FCSTD DOCUMENT  (FreeCAD 0.18R)
Label: StaveBracket
License: All rights reserved
LicenseURL: http://en.wikipedia.org/wiki/All_rights_reserved
objects: Sketcher::SketchObject×1
note: 1 computed .brp shape members not serialized (recipe doc carries the construction recipe); baked Part::Feature solids carry a one-line shape summary decoded from their .brp

FEATURE [Sketcher::SketchObject] Sketch  label="Sketch-Bracket"
  MapMode = 5
  expr: Constraints[64] = Constraints.b * 10
  expr: Constraints[61] = (Constraints.b - Constraints.bar_maj) * (2 - (1 + sqrt(5)) / 2)
  expr: Constraints.square = Constraints.b / (2 - (1 + sqrt(5)) / 2)
  expr: Constraints.bar_maj = Constraints.b * 2 / (1 + sqrt(5))
  sketch-geometry (26):
    g0: LineSegment [constr] StartX=-0.381966 StartY=1.8e-15 StartZ=0 EndX=0.618034 EndY=1.8e-15 EndZ=0
    g1: LineSegment [constr] StartX=0.618034 StartY=1.8e-15 StartZ=0 EndX=0 EndY=1.8e-15 EndZ=0
    g2: LineSegment StartX=-0.381966 StartY=1.8e-15 StartZ=0 EndX=-0.381966 EndY=1 EndZ=0
    g3: LineSegment [constr] StartX=-0.381966 StartY=1.8e-15 StartZ=0 EndX=2.23607 EndY=1.8e-15 EndZ=0
    g4: LineSegment [constr] StartX=2.23607 StartY=1.8e-15 StartZ=0 EndX=2.23607 EndY=2.61803 EndZ=0
    g5: LineSegment [constr] StartX=2.23607 StartY=2.61803 StartZ=0 EndX=-0.381966 EndY=2.61803 EndZ=0
    g6: LineSegment [constr] StartX=-0.381966 StartY=2.61803 StartZ=0 EndX=-0.381966 EndY=1.8e-15 EndZ=0
    g7: LineSegment [constr] StartX=0.618034 StartY=1.8e-15 StartZ=0 EndX=2.23607 EndY=2.61803 EndZ=0
    g8: LineSegment [constr] StartX=2.23607 StartY=2.61803 StartZ=0 EndX=-4.61803 EndY=6.8541 EndZ=0
    g9: LineSegment [constr] StartX=-0.381966 StartY=1.8e-15 StartZ=0 EndX=0.927051 EndY=1.30902 EndZ=0
    g10: LineSegment [constr] StartX=0.927051 StartY=1.30902 StartZ=0 EndX=2.23607 EndY=2.61803 EndZ=0
    g11: LineSegment [constr] StartX=0.927051 StartY=1.30902 StartZ=0 EndX=-4.61803 EndY=6.8541 EndZ=0
    g12: LineSegment [constr] StartX=-0.381966 StartY=1 StartZ=0 EndX=0.927051 EndY=1.80902 EndZ=0
    g13: LineSegment [constr] StartX=0.927051 StartY=1.80902 StartZ=0 EndX=2.23607 EndY=2.61803 EndZ=0
    g14: LineSegment [constr] StartX=0.927051 StartY=1.80902 StartZ=0 EndX=-2.5 EndY=7.3541 EndZ=0
    g15: LineSegment [constr] StartX=2.23607 StartY=2.61803 StartZ=0 EndX=-2.5 EndY=7.3541 EndZ=0
    g16: ArcOfCircle CenterX=-4.61803 CenterY=6.8541 CenterZ=0 NormalX=0 NormalY=0 NormalZ=1 AngleXU=0 Radius=8.05748 StartAngle=5.26596 EndAngle=5.72961
    g17: ArcOfCircle CenterX=-2.5 CenterY=7.3541 CenterZ=0 NormalX=0 NormalY=0 NormalZ=1 AngleXU=0 Radius=6.69781 StartAngle=5.03414 EndAngle=5.49779
    g18: LineSegment StartX=-0.381966 StartY=1 StartZ=0 EndX=0 EndY=1 EndZ=0
    g19: LineSegment StartX=0 StartY=1 StartZ=0 EndX=0 EndY=-10 EndZ=0
    g20: LineSegment StartX=0 StartY=-10 StartZ=0 EndX=-0.381966 EndY=-10 EndZ=0
    g21: LineSegment StartX=-0.381966 StartY=-10 StartZ=0 EndX=-0.381966 EndY=1 EndZ=0
    g22: LineSegment StartX=0.472136 StartY=1.8e-15 StartZ=0 EndX=0.618034 EndY=1.8e-15 EndZ=0
    g23: LineSegment StartX=0.618034 StartY=1.8e-15 StartZ=0 EndX=0.618034 EndY=-10 EndZ=0
    g24: LineSegment StartX=0.618034 StartY=-10 StartZ=0 EndX=0.472136 EndY=-10 EndZ=0
    g25: LineSegment StartX=0.472136 StartY=-10 StartZ=0 EndX=0.472136 EndY=1.8e-15 EndZ=0
  constraints (65):
    c: Coincident(g3,g4)
    c: Coincident(g4,g5)
    c: Coincident(g5,g6)
    c: Coincident(g6,g3)
    c: Horizontal(g3)
    c: Horizontal(g5)
    c: Vertical(g4)
    c: Vertical(g6)
    c: DistanceX(g0,g0) = 1  'b'
    c: DistanceX(g1,g1) = 0.618034  'bar_maj'
    c: DistanceX(g3,g3) = 2.61803  'square'
    c: Horizontal(g1)
    c: Horizontal(g0)
    c: Equal(g4,g3)
    c: Coincident(g1,g-1)
    c: Coincident(g0,g1)
    c: Coincident(g0,g3)
    c: Coincident(g0,g7)
    c: Coincident(g7,g4)
    c: Vertical(g2)
    c: Equal(g0,g2)
    c: Coincident(g2,g0)
    c: Coincident(g10,g4)
    c: Coincident(g9,g0)
    c: Tangent(g9,g10) = -1.5708
    c: Equal(g9,g10)
    c: Coincident(g12,g2)
    c: Coincident(g13,g4)
    c: Tangent(g12,g13) = -1.5708
    c: Coincident(g11,g9)
    c: Coincident(g14,g12)
    c: Coincident(g8,g4)
    c: Coincident(g11,g8)
    c: Coincident(g14,g15)
    c: Coincident(g15,g4)
    c: Coincident(g16,g8)
    c: Coincident(g14,g17)
    c: Coincident(g17,g4)
    c: Coincident(g17,g2)
    c: Coincident(g16,g4)
    c: Coincident(g16,g0)
    c: Perpendicular(g14,g12)
    c: Perpendicular(g8,g7)
    c: Perpendicular(g10,g15)
    c: Coincident(g18,g19)
    c: Coincident(g19,g20)
    c: Coincident(g20,g21)
    c: Coincident(g21,g18)
    c: Horizontal(g18)
    c: Horizontal(g20)
    c: Vertical(g19)
    c: Vertical(g21)
    c: Coincident(g22,g23)
    c: Coincident(g23,g24)
    c: Coincident(g24,g25)
    c: Coincident(g25,g22)
    c: Horizontal(g22)
    c: Vertical(g23)
    c: Vertical(g25)
    c: DistanceX(g-1,g18) = 0
    c: Coincident(g18,g2)
    c: DistanceX(g22,g22) = 0.145898
    c: Coincident(g22,g0)
    c: Tangent(g20,g24)
    c: DistanceY(g23,g23) = 10
